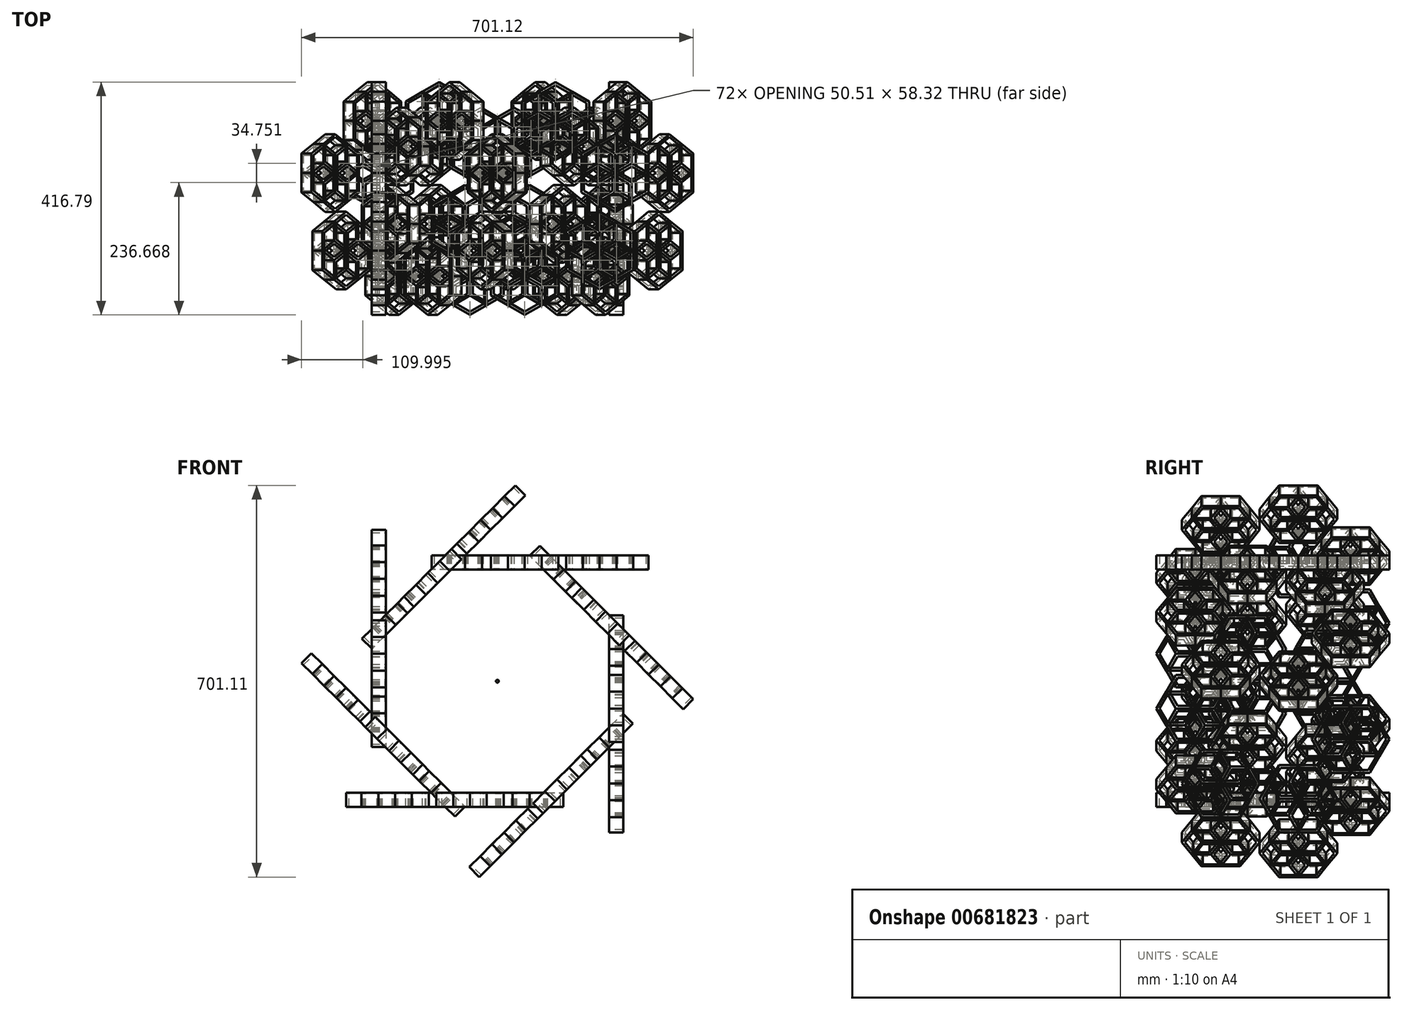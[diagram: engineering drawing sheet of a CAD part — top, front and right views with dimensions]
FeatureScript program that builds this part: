
annotation { "Feature Type Name" : "Feature", "Feature Type Description" : "" }
export const myFeature = defineFeature(function(context is Context, id is Id, definition is map)
    precondition{}
    {
        {
            var Q0;
            Q0=qCreatedBy(makeId("Top.planeOp"),FACE);
            var sketch = newSketch(context, id + "F0", { "sketchPlane" : qUnion([Q0])});
            skCircle(sketch, "E0.cCircle", {"center": v(0, 0) * mm, "radius": 34.75 * mm, "construction": true});
            skLineSegment(sketch, "E0.0", {"start": v(30.1, 17.38) * mm, "end": v(30.1, -17.38) * mm});
            skLineSegment(sketch, "E0.1", {"start": v(30.1, -17.38) * mm, "end": v(0, -34.75) * mm});
            skLineSegment(sketch, "E0.2", {"start": v(0, -34.75) * mm, "end": v(-30.1, -17.38) * mm});
            skLineSegment(sketch, "E0.3", {"start": v(-30.1, -17.38) * mm, "end": v(-30.1, 17.38) * mm});
            skLineSegment(sketch, "E0.4", {"start": v(-30.1, 17.38) * mm, "end": v(0, 34.75) * mm});
            skLineSegment(sketch, "E0.5", {"start": v(0, 34.75) * mm, "end": v(30.1, 17.38) * mm});
            skCircle(sketch, "E1.cCircle", {"center": v(0, 0) * mm, "radius": 29.16 * mm, "construction": true});
            skLineSegment(sketch, "E1.0", {"start": v(0, 29.16) * mm, "end": v(25.25, 14.58) * mm});
            skLineSegment(sketch, "E1.1", {"start": v(25.25, 14.58) * mm, "end": v(25.25, -14.58) * mm});
            skLineSegment(sketch, "E1.2", {"start": v(25.25, -14.58) * mm, "end": v(0, -29.16) * mm});
            skLineSegment(sketch, "E1.3", {"start": v(0, -29.16) * mm, "end": v(-25.25, -14.58) * mm});
            skLineSegment(sketch, "E1.4", {"start": v(-25.25, -14.58) * mm, "end": v(-25.25, 14.58) * mm});
            skLineSegment(sketch, "E1.5", {"start": v(-25.25, 14.58) * mm, "end": v(0, 29.16) * mm});
            skPoint(sketch, "E2", {"position": v(76.12, -75.54) * mm});
            skCircle(sketch, "E3", {"center": v(76.12, -75.54) * mm, "radius": 2.1 * mm});
            skSolve(sketch);
        }
        {
            var Q0;
            Q0=makeQuery(id+"F0.imprint","IMPRINT",FACE,{"disambiguationData":[TD([[makeQuery(id+"F0.imprint","IMPRINT",EDGE,{"derivedFrom":sQuery(id+"F0.wireOp",EDGE,"E0.0")}),-1.0]])]});
            extrude(context, id + "F1", {"entities" : qUnion([Q0]), "depth" : 25.4 * mm, "offsetDistance" : 25.4 * mm});
        }
        {
            var Q0;
            Q0=makeQuery(id+"F1.opExtrude","SWEPT_BODY",BODY,{"disambiguationData":[OSD([sQuery(id+"F0.wireOp",EDGE,"E0.0"),sQuery(id+"F0.wireOp",EDGE,"E0.1"),sQuery(id+"F0.wireOp",EDGE,"E0.2"),sQuery(id+"F0.wireOp",EDGE,"E0.3"),sQuery(id+"F0.wireOp",EDGE,"E0.4"),sQuery(id+"F0.wireOp",EDGE,"E0.5"),sQuery(id+"F0.wireOp",EDGE,"E1.0"),sQuery(id+"F0.wireOp",EDGE,"E1.1"),sQuery(id+"F0.wireOp",EDGE,"E1.2"),sQuery(id+"F0.wireOp",EDGE,"E1.3"),sQuery(id+"F0.wireOp",EDGE,"E1.4"),sQuery(id+"F0.wireOp",EDGE,"E1.5")])]});
            var Q1;
            Q1=makeQuery(id+"F1.opExtrude","SWEPT_EDGE",EDGE,{"disambiguationData":[OSD([sQuery(id+"F0.wireOp",EDGE,"E0.3"),sQuery(id+"F0.wireOp",EDGE,"E0.4")])]});
            circularPattern(context, id + "F2", {"entities" : qUnion([Q0]), "axis" : qUnion([Q1]), "angle" : 360 * degree, "instanceCount" : 6, "equalSpace" : true});
        }
        {
            var Q0;
            Q0=qCreatedBy(makeId("Top.planeOp"),FACE);
            var sketch = newSketch(context, id + "F3", { "sketchPlane" : qUnion([Q0])});
            skCircle(sketch, "E4", {"center": v(76.45, -75.87) * mm, "radius": 1.27 * mm});
            skSolve(sketch);
        }
        {
            var Q0;
            Q0=makeQuery(id+"F3.imprint","IMPRINT",FACE,{"disambiguationData":[TD([[makeQuery(id+"F3.imprint","IMPRINT",EDGE,{"derivedFrom":sQuery(id+"F3.wireOp",EDGE,"E4")}),1.0]])]});
            extrude(context, id + "F4", {"entities" : qUnion([Q0]), "depth" : 0.25 * mm, "offsetDistance" : 25.4 * mm});
        }
        {
            var Q0;
            Q0=makeQuery(id+"F1.opExtrude","SWEPT_BODY",BODY,{"disambiguationData":[OSD([sQuery(id+"F0.wireOp",EDGE,"E0.0"),sQuery(id+"F0.wireOp",EDGE,"E0.1"),sQuery(id+"F0.wireOp",EDGE,"E0.2"),sQuery(id+"F0.wireOp",EDGE,"E0.3"),sQuery(id+"F0.wireOp",EDGE,"E0.4"),sQuery(id+"F0.wireOp",EDGE,"E0.5"),sQuery(id+"F0.wireOp",EDGE,"E1.0"),sQuery(id+"F0.wireOp",EDGE,"E1.1"),sQuery(id+"F0.wireOp",EDGE,"E1.2"),sQuery(id+"F0.wireOp",EDGE,"E1.3"),sQuery(id+"F0.wireOp",EDGE,"E1.4"),sQuery(id+"F0.wireOp",EDGE,"E1.5")])]});
            var Q1;
            Q1=makeQuery(id+"F2.opPattern","COPY",BODY,{"derivedFrom":makeQuery(id+"F1.opExtrude","SWEPT_BODY",BODY,{"disambiguationData":[OSD([sQuery(id+"F0.wireOp",EDGE,"E0.0"),sQuery(id+"F0.wireOp",EDGE,"E0.1"),sQuery(id+"F0.wireOp",EDGE,"E0.2"),sQuery(id+"F0.wireOp",EDGE,"E0.3"),sQuery(id+"F0.wireOp",EDGE,"E0.4"),sQuery(id+"F0.wireOp",EDGE,"E0.5"),sQuery(id+"F0.wireOp",EDGE,"E1.0"),sQuery(id+"F0.wireOp",EDGE,"E1.1"),sQuery(id+"F0.wireOp",EDGE,"E1.2"),sQuery(id+"F0.wireOp",EDGE,"E1.3"),sQuery(id+"F0.wireOp",EDGE,"E1.4"),sQuery(id+"F0.wireOp",EDGE,"E1.5")])]}),"instanceName":"1"});
            var Q2;
            Q2=makeQuery(id+"F2.opPattern","COPY",BODY,{"derivedFrom":makeQuery(id+"F1.opExtrude","SWEPT_BODY",BODY,{"disambiguationData":[OSD([sQuery(id+"F0.wireOp",EDGE,"E0.0"),sQuery(id+"F0.wireOp",EDGE,"E0.1"),sQuery(id+"F0.wireOp",EDGE,"E0.2"),sQuery(id+"F0.wireOp",EDGE,"E0.3"),sQuery(id+"F0.wireOp",EDGE,"E0.4"),sQuery(id+"F0.wireOp",EDGE,"E0.5"),sQuery(id+"F0.wireOp",EDGE,"E1.0"),sQuery(id+"F0.wireOp",EDGE,"E1.1"),sQuery(id+"F0.wireOp",EDGE,"E1.2"),sQuery(id+"F0.wireOp",EDGE,"E1.3"),sQuery(id+"F0.wireOp",EDGE,"E1.4"),sQuery(id+"F0.wireOp",EDGE,"E1.5")])]}),"instanceName":"2"});
            var Q3;
            Q3=makeQuery(id+"F2.opPattern","COPY",BODY,{"derivedFrom":makeQuery(id+"F1.opExtrude","SWEPT_BODY",BODY,{"disambiguationData":[OSD([sQuery(id+"F0.wireOp",EDGE,"E0.0"),sQuery(id+"F0.wireOp",EDGE,"E0.1"),sQuery(id+"F0.wireOp",EDGE,"E0.2"),sQuery(id+"F0.wireOp",EDGE,"E0.3"),sQuery(id+"F0.wireOp",EDGE,"E0.4"),sQuery(id+"F0.wireOp",EDGE,"E0.5"),sQuery(id+"F0.wireOp",EDGE,"E1.0"),sQuery(id+"F0.wireOp",EDGE,"E1.1"),sQuery(id+"F0.wireOp",EDGE,"E1.2"),sQuery(id+"F0.wireOp",EDGE,"E1.3"),sQuery(id+"F0.wireOp",EDGE,"E1.4"),sQuery(id+"F0.wireOp",EDGE,"E1.5")])]}),"instanceName":"3"});
            var Q4;
            Q4=makeQuery(id+"F2.opPattern","COPY",BODY,{"derivedFrom":makeQuery(id+"F1.opExtrude","SWEPT_BODY",BODY,{"disambiguationData":[OSD([sQuery(id+"F0.wireOp",EDGE,"E0.0"),sQuery(id+"F0.wireOp",EDGE,"E0.1"),sQuery(id+"F0.wireOp",EDGE,"E0.2"),sQuery(id+"F0.wireOp",EDGE,"E0.3"),sQuery(id+"F0.wireOp",EDGE,"E0.4"),sQuery(id+"F0.wireOp",EDGE,"E0.5"),sQuery(id+"F0.wireOp",EDGE,"E1.0"),sQuery(id+"F0.wireOp",EDGE,"E1.1"),sQuery(id+"F0.wireOp",EDGE,"E1.2"),sQuery(id+"F0.wireOp",EDGE,"E1.3"),sQuery(id+"F0.wireOp",EDGE,"E1.4"),sQuery(id+"F0.wireOp",EDGE,"E1.5")])]}),"instanceName":"4"});
            var Q5;
            Q5=makeQuery(id+"F2.opPattern","COPY",BODY,{"derivedFrom":makeQuery(id+"F1.opExtrude","SWEPT_BODY",BODY,{"disambiguationData":[OSD([sQuery(id+"F0.wireOp",EDGE,"E0.0"),sQuery(id+"F0.wireOp",EDGE,"E0.1"),sQuery(id+"F0.wireOp",EDGE,"E0.2"),sQuery(id+"F0.wireOp",EDGE,"E0.3"),sQuery(id+"F0.wireOp",EDGE,"E0.4"),sQuery(id+"F0.wireOp",EDGE,"E0.5"),sQuery(id+"F0.wireOp",EDGE,"E1.0"),sQuery(id+"F0.wireOp",EDGE,"E1.1"),sQuery(id+"F0.wireOp",EDGE,"E1.2"),sQuery(id+"F0.wireOp",EDGE,"E1.3"),sQuery(id+"F0.wireOp",EDGE,"E1.4"),sQuery(id+"F0.wireOp",EDGE,"E1.5")])]}),"instanceName":"5"});
            var Q6;
            Q6=makeQuery(id+"F4.opExtrude","CAP_EDGE",EDGE,{"disambiguationData":[OSD([sQuery(id+"F3.wireOp",EDGE,"E4")])],"isStart":false});
            circularPattern(context, id + "F5", {"entities" : qUnion([Q0, Q1, Q2, Q3, Q4, Q5]), "axis" : qUnion([Q6]), "angle" : 360 * degree, "instanceCount" : 6, "oppositeDirection" : true, "equalSpace" : true});
        }
        {
            var Q0;
            Q0=qCreatedBy(makeId("Front.planeOp"),FACE);
            var sketch = newSketch(context, id + "F6", { "sketchPlane" : qUnion([Q0])});
            skCircle(sketch, "E5", {"center": v(0, -199.7) * mm, "radius": 2.54 * mm});
            skSolve(sketch);
        }
        {
            var Q0;
            Q0=makeQuery(id+"F6.imprint","IMPRINT",FACE,{"disambiguationData":[TD([[makeQuery(id+"F6.imprint","IMPRINT",EDGE,{"derivedFrom":sQuery(id+"F6.wireOp",EDGE,"E5")}),1.0]])]});
            extrude(context, id + "F7", {"entities" : qUnion([Q0]), "depth" : 0.25 * mm, "offsetDistance" : 25.4 * mm});
        }
        {
            var Q0;
            Q0=makeQuery(id+"F2.opPattern","COPY",BODY,{"derivedFrom":makeQuery(id+"F1.opExtrude","SWEPT_BODY",BODY,{"disambiguationData":[OSD([sQuery(id+"F0.wireOp",EDGE,"E0.0"),sQuery(id+"F0.wireOp",EDGE,"E0.1"),sQuery(id+"F0.wireOp",EDGE,"E0.2"),sQuery(id+"F0.wireOp",EDGE,"E0.3"),sQuery(id+"F0.wireOp",EDGE,"E0.4"),sQuery(id+"F0.wireOp",EDGE,"E0.5"),sQuery(id+"F0.wireOp",EDGE,"E1.0"),sQuery(id+"F0.wireOp",EDGE,"E1.1"),sQuery(id+"F0.wireOp",EDGE,"E1.2"),sQuery(id+"F0.wireOp",EDGE,"E1.3"),sQuery(id+"F0.wireOp",EDGE,"E1.4"),sQuery(id+"F0.wireOp",EDGE,"E1.5")])]}),"instanceName":"1"});
            var Q1;
            Q1=makeQuery(id+"F2.opPattern","COPY",BODY,{"derivedFrom":makeQuery(id+"F1.opExtrude","SWEPT_BODY",BODY,{"disambiguationData":[OSD([sQuery(id+"F0.wireOp",EDGE,"E0.0"),sQuery(id+"F0.wireOp",EDGE,"E0.1"),sQuery(id+"F0.wireOp",EDGE,"E0.2"),sQuery(id+"F0.wireOp",EDGE,"E0.3"),sQuery(id+"F0.wireOp",EDGE,"E0.4"),sQuery(id+"F0.wireOp",EDGE,"E0.5"),sQuery(id+"F0.wireOp",EDGE,"E1.0"),sQuery(id+"F0.wireOp",EDGE,"E1.1"),sQuery(id+"F0.wireOp",EDGE,"E1.2"),sQuery(id+"F0.wireOp",EDGE,"E1.3"),sQuery(id+"F0.wireOp",EDGE,"E1.4"),sQuery(id+"F0.wireOp",EDGE,"E1.5")])]}),"instanceName":"4"});
            var Q2;
            Q2=makeQuery(id+"F1.opExtrude","SWEPT_BODY",BODY,{"disambiguationData":[OSD([sQuery(id+"F0.wireOp",EDGE,"E0.0"),sQuery(id+"F0.wireOp",EDGE,"E0.1"),sQuery(id+"F0.wireOp",EDGE,"E0.2"),sQuery(id+"F0.wireOp",EDGE,"E0.3"),sQuery(id+"F0.wireOp",EDGE,"E0.4"),sQuery(id+"F0.wireOp",EDGE,"E0.5"),sQuery(id+"F0.wireOp",EDGE,"E1.0"),sQuery(id+"F0.wireOp",EDGE,"E1.1"),sQuery(id+"F0.wireOp",EDGE,"E1.2"),sQuery(id+"F0.wireOp",EDGE,"E1.3"),sQuery(id+"F0.wireOp",EDGE,"E1.4"),sQuery(id+"F0.wireOp",EDGE,"E1.5")])]});
            var Q3;
            Q3=makeQuery(id+"F2.opPattern","COPY",BODY,{"derivedFrom":makeQuery(id+"F1.opExtrude","SWEPT_BODY",BODY,{"disambiguationData":[OSD([sQuery(id+"F0.wireOp",EDGE,"E0.0"),sQuery(id+"F0.wireOp",EDGE,"E0.1"),sQuery(id+"F0.wireOp",EDGE,"E0.2"),sQuery(id+"F0.wireOp",EDGE,"E0.3"),sQuery(id+"F0.wireOp",EDGE,"E0.4"),sQuery(id+"F0.wireOp",EDGE,"E0.5"),sQuery(id+"F0.wireOp",EDGE,"E1.0"),sQuery(id+"F0.wireOp",EDGE,"E1.1"),sQuery(id+"F0.wireOp",EDGE,"E1.2"),sQuery(id+"F0.wireOp",EDGE,"E1.3"),sQuery(id+"F0.wireOp",EDGE,"E1.4"),sQuery(id+"F0.wireOp",EDGE,"E1.5")])]}),"instanceName":"2"});
            var Q4;
            Q4=makeQuery(id+"F2.opPattern","COPY",BODY,{"derivedFrom":makeQuery(id+"F1.opExtrude","SWEPT_BODY",BODY,{"disambiguationData":[OSD([sQuery(id+"F0.wireOp",EDGE,"E0.0"),sQuery(id+"F0.wireOp",EDGE,"E0.1"),sQuery(id+"F0.wireOp",EDGE,"E0.2"),sQuery(id+"F0.wireOp",EDGE,"E0.3"),sQuery(id+"F0.wireOp",EDGE,"E0.4"),sQuery(id+"F0.wireOp",EDGE,"E0.5"),sQuery(id+"F0.wireOp",EDGE,"E1.0"),sQuery(id+"F0.wireOp",EDGE,"E1.1"),sQuery(id+"F0.wireOp",EDGE,"E1.2"),sQuery(id+"F0.wireOp",EDGE,"E1.3"),sQuery(id+"F0.wireOp",EDGE,"E1.4"),sQuery(id+"F0.wireOp",EDGE,"E1.5")])]}),"instanceName":"3"});
            var Q5;
            Q5=makeQuery(id+"F2.opPattern","COPY",BODY,{"derivedFrom":makeQuery(id+"F1.opExtrude","SWEPT_BODY",BODY,{"disambiguationData":[OSD([sQuery(id+"F0.wireOp",EDGE,"E0.0"),sQuery(id+"F0.wireOp",EDGE,"E0.1"),sQuery(id+"F0.wireOp",EDGE,"E0.2"),sQuery(id+"F0.wireOp",EDGE,"E0.3"),sQuery(id+"F0.wireOp",EDGE,"E0.4"),sQuery(id+"F0.wireOp",EDGE,"E0.5"),sQuery(id+"F0.wireOp",EDGE,"E1.0"),sQuery(id+"F0.wireOp",EDGE,"E1.1"),sQuery(id+"F0.wireOp",EDGE,"E1.2"),sQuery(id+"F0.wireOp",EDGE,"E1.3"),sQuery(id+"F0.wireOp",EDGE,"E1.4"),sQuery(id+"F0.wireOp",EDGE,"E1.5")])]}),"instanceName":"5"});
            var Q6;
            Q6=makeQuery(id+"F5.opPattern","COPY",BODY,{"derivedFrom":makeQuery(id+"F1.opExtrude","SWEPT_BODY",BODY,{"disambiguationData":[OSD([sQuery(id+"F0.wireOp",EDGE,"E0.0"),sQuery(id+"F0.wireOp",EDGE,"E0.1"),sQuery(id+"F0.wireOp",EDGE,"E0.2"),sQuery(id+"F0.wireOp",EDGE,"E0.3"),sQuery(id+"F0.wireOp",EDGE,"E0.4"),sQuery(id+"F0.wireOp",EDGE,"E0.5"),sQuery(id+"F0.wireOp",EDGE,"E1.0"),sQuery(id+"F0.wireOp",EDGE,"E1.1"),sQuery(id+"F0.wireOp",EDGE,"E1.2"),sQuery(id+"F0.wireOp",EDGE,"E1.3"),sQuery(id+"F0.wireOp",EDGE,"E1.4"),sQuery(id+"F0.wireOp",EDGE,"E1.5")])]}),"instanceName":"1"});
            var Q7;
            Q7=makeQuery(id+"F4.opExtrude","SWEPT_BODY",BODY,{"disambiguationData":[OSD([sQuery(id+"F3.wireOp",EDGE,"E4")])]});
            var Q8;
            Q8=makeQuery(id+"F5.opPattern","COPY",BODY,{"derivedFrom":makeQuery(id+"F2.opPattern","COPY",BODY,{"derivedFrom":makeQuery(id+"F1.opExtrude","SWEPT_BODY",BODY,{"disambiguationData":[OSD([sQuery(id+"F0.wireOp",EDGE,"E0.0"),sQuery(id+"F0.wireOp",EDGE,"E0.1"),sQuery(id+"F0.wireOp",EDGE,"E0.2"),sQuery(id+"F0.wireOp",EDGE,"E0.3"),sQuery(id+"F0.wireOp",EDGE,"E0.4"),sQuery(id+"F0.wireOp",EDGE,"E0.5"),sQuery(id+"F0.wireOp",EDGE,"E1.0"),sQuery(id+"F0.wireOp",EDGE,"E1.1"),sQuery(id+"F0.wireOp",EDGE,"E1.2"),sQuery(id+"F0.wireOp",EDGE,"E1.3"),sQuery(id+"F0.wireOp",EDGE,"E1.4"),sQuery(id+"F0.wireOp",EDGE,"E1.5")])]}),"instanceName":"1"}),"instanceName":"1"});
            var Q9;
            Q9=makeQuery(id+"F5.opPattern","COPY",BODY,{"derivedFrom":makeQuery(id+"F2.opPattern","COPY",BODY,{"derivedFrom":makeQuery(id+"F1.opExtrude","SWEPT_BODY",BODY,{"disambiguationData":[OSD([sQuery(id+"F0.wireOp",EDGE,"E0.0"),sQuery(id+"F0.wireOp",EDGE,"E0.1"),sQuery(id+"F0.wireOp",EDGE,"E0.2"),sQuery(id+"F0.wireOp",EDGE,"E0.3"),sQuery(id+"F0.wireOp",EDGE,"E0.4"),sQuery(id+"F0.wireOp",EDGE,"E0.5"),sQuery(id+"F0.wireOp",EDGE,"E1.0"),sQuery(id+"F0.wireOp",EDGE,"E1.1"),sQuery(id+"F0.wireOp",EDGE,"E1.2"),sQuery(id+"F0.wireOp",EDGE,"E1.3"),sQuery(id+"F0.wireOp",EDGE,"E1.4"),sQuery(id+"F0.wireOp",EDGE,"E1.5")])]}),"instanceName":"2"}),"instanceName":"1"});
            var Q10;
            Q10=makeQuery(id+"F5.opPattern","COPY",BODY,{"derivedFrom":makeQuery(id+"F2.opPattern","COPY",BODY,{"derivedFrom":makeQuery(id+"F1.opExtrude","SWEPT_BODY",BODY,{"disambiguationData":[OSD([sQuery(id+"F0.wireOp",EDGE,"E0.0"),sQuery(id+"F0.wireOp",EDGE,"E0.1"),sQuery(id+"F0.wireOp",EDGE,"E0.2"),sQuery(id+"F0.wireOp",EDGE,"E0.3"),sQuery(id+"F0.wireOp",EDGE,"E0.4"),sQuery(id+"F0.wireOp",EDGE,"E0.5"),sQuery(id+"F0.wireOp",EDGE,"E1.0"),sQuery(id+"F0.wireOp",EDGE,"E1.1"),sQuery(id+"F0.wireOp",EDGE,"E1.2"),sQuery(id+"F0.wireOp",EDGE,"E1.3"),sQuery(id+"F0.wireOp",EDGE,"E1.4"),sQuery(id+"F0.wireOp",EDGE,"E1.5")])]}),"instanceName":"3"}),"instanceName":"1"});
            var Q11;
            Q11=makeQuery(id+"F5.opPattern","COPY",BODY,{"derivedFrom":makeQuery(id+"F2.opPattern","COPY",BODY,{"derivedFrom":makeQuery(id+"F1.opExtrude","SWEPT_BODY",BODY,{"disambiguationData":[OSD([sQuery(id+"F0.wireOp",EDGE,"E0.0"),sQuery(id+"F0.wireOp",EDGE,"E0.1"),sQuery(id+"F0.wireOp",EDGE,"E0.2"),sQuery(id+"F0.wireOp",EDGE,"E0.3"),sQuery(id+"F0.wireOp",EDGE,"E0.4"),sQuery(id+"F0.wireOp",EDGE,"E0.5"),sQuery(id+"F0.wireOp",EDGE,"E1.0"),sQuery(id+"F0.wireOp",EDGE,"E1.1"),sQuery(id+"F0.wireOp",EDGE,"E1.2"),sQuery(id+"F0.wireOp",EDGE,"E1.3"),sQuery(id+"F0.wireOp",EDGE,"E1.4"),sQuery(id+"F0.wireOp",EDGE,"E1.5")])]}),"instanceName":"4"}),"instanceName":"1"});
            var Q12;
            Q12=makeQuery(id+"F5.opPattern","COPY",BODY,{"derivedFrom":makeQuery(id+"F2.opPattern","COPY",BODY,{"derivedFrom":makeQuery(id+"F1.opExtrude","SWEPT_BODY",BODY,{"disambiguationData":[OSD([sQuery(id+"F0.wireOp",EDGE,"E0.0"),sQuery(id+"F0.wireOp",EDGE,"E0.1"),sQuery(id+"F0.wireOp",EDGE,"E0.2"),sQuery(id+"F0.wireOp",EDGE,"E0.3"),sQuery(id+"F0.wireOp",EDGE,"E0.4"),sQuery(id+"F0.wireOp",EDGE,"E0.5"),sQuery(id+"F0.wireOp",EDGE,"E1.0"),sQuery(id+"F0.wireOp",EDGE,"E1.1"),sQuery(id+"F0.wireOp",EDGE,"E1.2"),sQuery(id+"F0.wireOp",EDGE,"E1.3"),sQuery(id+"F0.wireOp",EDGE,"E1.4"),sQuery(id+"F0.wireOp",EDGE,"E1.5")])]}),"instanceName":"5"}),"instanceName":"1"});
            var Q13;
            Q13=makeQuery(id+"F5.opPattern","COPY",BODY,{"derivedFrom":makeQuery(id+"F1.opExtrude","SWEPT_BODY",BODY,{"disambiguationData":[OSD([sQuery(id+"F0.wireOp",EDGE,"E0.0"),sQuery(id+"F0.wireOp",EDGE,"E0.1"),sQuery(id+"F0.wireOp",EDGE,"E0.2"),sQuery(id+"F0.wireOp",EDGE,"E0.3"),sQuery(id+"F0.wireOp",EDGE,"E0.4"),sQuery(id+"F0.wireOp",EDGE,"E0.5"),sQuery(id+"F0.wireOp",EDGE,"E1.0"),sQuery(id+"F0.wireOp",EDGE,"E1.1"),sQuery(id+"F0.wireOp",EDGE,"E1.2"),sQuery(id+"F0.wireOp",EDGE,"E1.3"),sQuery(id+"F0.wireOp",EDGE,"E1.4"),sQuery(id+"F0.wireOp",EDGE,"E1.5")])]}),"instanceName":"2"});
            var Q14;
            Q14=makeQuery(id+"F5.opPattern","COPY",BODY,{"derivedFrom":makeQuery(id+"F2.opPattern","COPY",BODY,{"derivedFrom":makeQuery(id+"F1.opExtrude","SWEPT_BODY",BODY,{"disambiguationData":[OSD([sQuery(id+"F0.wireOp",EDGE,"E0.0"),sQuery(id+"F0.wireOp",EDGE,"E0.1"),sQuery(id+"F0.wireOp",EDGE,"E0.2"),sQuery(id+"F0.wireOp",EDGE,"E0.3"),sQuery(id+"F0.wireOp",EDGE,"E0.4"),sQuery(id+"F0.wireOp",EDGE,"E0.5"),sQuery(id+"F0.wireOp",EDGE,"E1.0"),sQuery(id+"F0.wireOp",EDGE,"E1.1"),sQuery(id+"F0.wireOp",EDGE,"E1.2"),sQuery(id+"F0.wireOp",EDGE,"E1.3"),sQuery(id+"F0.wireOp",EDGE,"E1.4"),sQuery(id+"F0.wireOp",EDGE,"E1.5")])]}),"instanceName":"1"}),"instanceName":"2"});
            var Q15;
            Q15=makeQuery(id+"F5.opPattern","COPY",BODY,{"derivedFrom":makeQuery(id+"F2.opPattern","COPY",BODY,{"derivedFrom":makeQuery(id+"F1.opExtrude","SWEPT_BODY",BODY,{"disambiguationData":[OSD([sQuery(id+"F0.wireOp",EDGE,"E0.0"),sQuery(id+"F0.wireOp",EDGE,"E0.1"),sQuery(id+"F0.wireOp",EDGE,"E0.2"),sQuery(id+"F0.wireOp",EDGE,"E0.3"),sQuery(id+"F0.wireOp",EDGE,"E0.4"),sQuery(id+"F0.wireOp",EDGE,"E0.5"),sQuery(id+"F0.wireOp",EDGE,"E1.0"),sQuery(id+"F0.wireOp",EDGE,"E1.1"),sQuery(id+"F0.wireOp",EDGE,"E1.2"),sQuery(id+"F0.wireOp",EDGE,"E1.3"),sQuery(id+"F0.wireOp",EDGE,"E1.4"),sQuery(id+"F0.wireOp",EDGE,"E1.5")])]}),"instanceName":"2"}),"instanceName":"2"});
            var Q16;
            Q16=makeQuery(id+"F5.opPattern","COPY",BODY,{"derivedFrom":makeQuery(id+"F2.opPattern","COPY",BODY,{"derivedFrom":makeQuery(id+"F1.opExtrude","SWEPT_BODY",BODY,{"disambiguationData":[OSD([sQuery(id+"F0.wireOp",EDGE,"E0.0"),sQuery(id+"F0.wireOp",EDGE,"E0.1"),sQuery(id+"F0.wireOp",EDGE,"E0.2"),sQuery(id+"F0.wireOp",EDGE,"E0.3"),sQuery(id+"F0.wireOp",EDGE,"E0.4"),sQuery(id+"F0.wireOp",EDGE,"E0.5"),sQuery(id+"F0.wireOp",EDGE,"E1.0"),sQuery(id+"F0.wireOp",EDGE,"E1.1"),sQuery(id+"F0.wireOp",EDGE,"E1.2"),sQuery(id+"F0.wireOp",EDGE,"E1.3"),sQuery(id+"F0.wireOp",EDGE,"E1.4"),sQuery(id+"F0.wireOp",EDGE,"E1.5")])]}),"instanceName":"3"}),"instanceName":"2"});
            var Q17;
            Q17=makeQuery(id+"F5.opPattern","COPY",BODY,{"derivedFrom":makeQuery(id+"F2.opPattern","COPY",BODY,{"derivedFrom":makeQuery(id+"F1.opExtrude","SWEPT_BODY",BODY,{"disambiguationData":[OSD([sQuery(id+"F0.wireOp",EDGE,"E0.0"),sQuery(id+"F0.wireOp",EDGE,"E0.1"),sQuery(id+"F0.wireOp",EDGE,"E0.2"),sQuery(id+"F0.wireOp",EDGE,"E0.3"),sQuery(id+"F0.wireOp",EDGE,"E0.4"),sQuery(id+"F0.wireOp",EDGE,"E0.5"),sQuery(id+"F0.wireOp",EDGE,"E1.0"),sQuery(id+"F0.wireOp",EDGE,"E1.1"),sQuery(id+"F0.wireOp",EDGE,"E1.2"),sQuery(id+"F0.wireOp",EDGE,"E1.3"),sQuery(id+"F0.wireOp",EDGE,"E1.4"),sQuery(id+"F0.wireOp",EDGE,"E1.5")])]}),"instanceName":"4"}),"instanceName":"2"});
            var Q18;
            Q18=makeQuery(id+"F5.opPattern","COPY",BODY,{"derivedFrom":makeQuery(id+"F2.opPattern","COPY",BODY,{"derivedFrom":makeQuery(id+"F1.opExtrude","SWEPT_BODY",BODY,{"disambiguationData":[OSD([sQuery(id+"F0.wireOp",EDGE,"E0.0"),sQuery(id+"F0.wireOp",EDGE,"E0.1"),sQuery(id+"F0.wireOp",EDGE,"E0.2"),sQuery(id+"F0.wireOp",EDGE,"E0.3"),sQuery(id+"F0.wireOp",EDGE,"E0.4"),sQuery(id+"F0.wireOp",EDGE,"E0.5"),sQuery(id+"F0.wireOp",EDGE,"E1.0"),sQuery(id+"F0.wireOp",EDGE,"E1.1"),sQuery(id+"F0.wireOp",EDGE,"E1.2"),sQuery(id+"F0.wireOp",EDGE,"E1.3"),sQuery(id+"F0.wireOp",EDGE,"E1.4"),sQuery(id+"F0.wireOp",EDGE,"E1.5")])]}),"instanceName":"5"}),"instanceName":"2"});
            var Q19;
            Q19=makeQuery(id+"F5.opPattern","COPY",BODY,{"derivedFrom":makeQuery(id+"F1.opExtrude","SWEPT_BODY",BODY,{"disambiguationData":[OSD([sQuery(id+"F0.wireOp",EDGE,"E0.0"),sQuery(id+"F0.wireOp",EDGE,"E0.1"),sQuery(id+"F0.wireOp",EDGE,"E0.2"),sQuery(id+"F0.wireOp",EDGE,"E0.3"),sQuery(id+"F0.wireOp",EDGE,"E0.4"),sQuery(id+"F0.wireOp",EDGE,"E0.5"),sQuery(id+"F0.wireOp",EDGE,"E1.0"),sQuery(id+"F0.wireOp",EDGE,"E1.1"),sQuery(id+"F0.wireOp",EDGE,"E1.2"),sQuery(id+"F0.wireOp",EDGE,"E1.3"),sQuery(id+"F0.wireOp",EDGE,"E1.4"),sQuery(id+"F0.wireOp",EDGE,"E1.5")])]}),"instanceName":"3"});
            var Q20;
            Q20=makeQuery(id+"F5.opPattern","COPY",BODY,{"derivedFrom":makeQuery(id+"F2.opPattern","COPY",BODY,{"derivedFrom":makeQuery(id+"F1.opExtrude","SWEPT_BODY",BODY,{"disambiguationData":[OSD([sQuery(id+"F0.wireOp",EDGE,"E0.0"),sQuery(id+"F0.wireOp",EDGE,"E0.1"),sQuery(id+"F0.wireOp",EDGE,"E0.2"),sQuery(id+"F0.wireOp",EDGE,"E0.3"),sQuery(id+"F0.wireOp",EDGE,"E0.4"),sQuery(id+"F0.wireOp",EDGE,"E0.5"),sQuery(id+"F0.wireOp",EDGE,"E1.0"),sQuery(id+"F0.wireOp",EDGE,"E1.1"),sQuery(id+"F0.wireOp",EDGE,"E1.2"),sQuery(id+"F0.wireOp",EDGE,"E1.3"),sQuery(id+"F0.wireOp",EDGE,"E1.4"),sQuery(id+"F0.wireOp",EDGE,"E1.5")])]}),"instanceName":"1"}),"instanceName":"3"});
            var Q21;
            Q21=makeQuery(id+"F5.opPattern","COPY",BODY,{"derivedFrom":makeQuery(id+"F2.opPattern","COPY",BODY,{"derivedFrom":makeQuery(id+"F1.opExtrude","SWEPT_BODY",BODY,{"disambiguationData":[OSD([sQuery(id+"F0.wireOp",EDGE,"E0.0"),sQuery(id+"F0.wireOp",EDGE,"E0.1"),sQuery(id+"F0.wireOp",EDGE,"E0.2"),sQuery(id+"F0.wireOp",EDGE,"E0.3"),sQuery(id+"F0.wireOp",EDGE,"E0.4"),sQuery(id+"F0.wireOp",EDGE,"E0.5"),sQuery(id+"F0.wireOp",EDGE,"E1.0"),sQuery(id+"F0.wireOp",EDGE,"E1.1"),sQuery(id+"F0.wireOp",EDGE,"E1.2"),sQuery(id+"F0.wireOp",EDGE,"E1.3"),sQuery(id+"F0.wireOp",EDGE,"E1.4"),sQuery(id+"F0.wireOp",EDGE,"E1.5")])]}),"instanceName":"2"}),"instanceName":"3"});
            var Q22;
            Q22=makeQuery(id+"F5.opPattern","COPY",BODY,{"derivedFrom":makeQuery(id+"F2.opPattern","COPY",BODY,{"derivedFrom":makeQuery(id+"F1.opExtrude","SWEPT_BODY",BODY,{"disambiguationData":[OSD([sQuery(id+"F0.wireOp",EDGE,"E0.0"),sQuery(id+"F0.wireOp",EDGE,"E0.1"),sQuery(id+"F0.wireOp",EDGE,"E0.2"),sQuery(id+"F0.wireOp",EDGE,"E0.3"),sQuery(id+"F0.wireOp",EDGE,"E0.4"),sQuery(id+"F0.wireOp",EDGE,"E0.5"),sQuery(id+"F0.wireOp",EDGE,"E1.0"),sQuery(id+"F0.wireOp",EDGE,"E1.1"),sQuery(id+"F0.wireOp",EDGE,"E1.2"),sQuery(id+"F0.wireOp",EDGE,"E1.3"),sQuery(id+"F0.wireOp",EDGE,"E1.4"),sQuery(id+"F0.wireOp",EDGE,"E1.5")])]}),"instanceName":"3"}),"instanceName":"3"});
            var Q23;
            Q23=makeQuery(id+"F5.opPattern","COPY",BODY,{"derivedFrom":makeQuery(id+"F2.opPattern","COPY",BODY,{"derivedFrom":makeQuery(id+"F1.opExtrude","SWEPT_BODY",BODY,{"disambiguationData":[OSD([sQuery(id+"F0.wireOp",EDGE,"E0.0"),sQuery(id+"F0.wireOp",EDGE,"E0.1"),sQuery(id+"F0.wireOp",EDGE,"E0.2"),sQuery(id+"F0.wireOp",EDGE,"E0.3"),sQuery(id+"F0.wireOp",EDGE,"E0.4"),sQuery(id+"F0.wireOp",EDGE,"E0.5"),sQuery(id+"F0.wireOp",EDGE,"E1.0"),sQuery(id+"F0.wireOp",EDGE,"E1.1"),sQuery(id+"F0.wireOp",EDGE,"E1.2"),sQuery(id+"F0.wireOp",EDGE,"E1.3"),sQuery(id+"F0.wireOp",EDGE,"E1.4"),sQuery(id+"F0.wireOp",EDGE,"E1.5")])]}),"instanceName":"4"}),"instanceName":"3"});
            var Q24;
            Q24=makeQuery(id+"F5.opPattern","COPY",BODY,{"derivedFrom":makeQuery(id+"F2.opPattern","COPY",BODY,{"derivedFrom":makeQuery(id+"F1.opExtrude","SWEPT_BODY",BODY,{"disambiguationData":[OSD([sQuery(id+"F0.wireOp",EDGE,"E0.0"),sQuery(id+"F0.wireOp",EDGE,"E0.1"),sQuery(id+"F0.wireOp",EDGE,"E0.2"),sQuery(id+"F0.wireOp",EDGE,"E0.3"),sQuery(id+"F0.wireOp",EDGE,"E0.4"),sQuery(id+"F0.wireOp",EDGE,"E0.5"),sQuery(id+"F0.wireOp",EDGE,"E1.0"),sQuery(id+"F0.wireOp",EDGE,"E1.1"),sQuery(id+"F0.wireOp",EDGE,"E1.2"),sQuery(id+"F0.wireOp",EDGE,"E1.3"),sQuery(id+"F0.wireOp",EDGE,"E1.4"),sQuery(id+"F0.wireOp",EDGE,"E1.5")])]}),"instanceName":"5"}),"instanceName":"3"});
            var Q25;
            Q25=makeQuery(id+"F5.opPattern","COPY",BODY,{"derivedFrom":makeQuery(id+"F1.opExtrude","SWEPT_BODY",BODY,{"disambiguationData":[OSD([sQuery(id+"F0.wireOp",EDGE,"E0.0"),sQuery(id+"F0.wireOp",EDGE,"E0.1"),sQuery(id+"F0.wireOp",EDGE,"E0.2"),sQuery(id+"F0.wireOp",EDGE,"E0.3"),sQuery(id+"F0.wireOp",EDGE,"E0.4"),sQuery(id+"F0.wireOp",EDGE,"E0.5"),sQuery(id+"F0.wireOp",EDGE,"E1.0"),sQuery(id+"F0.wireOp",EDGE,"E1.1"),sQuery(id+"F0.wireOp",EDGE,"E1.2"),sQuery(id+"F0.wireOp",EDGE,"E1.3"),sQuery(id+"F0.wireOp",EDGE,"E1.4"),sQuery(id+"F0.wireOp",EDGE,"E1.5")])]}),"instanceName":"4"});
            var Q26;
            Q26=makeQuery(id+"F5.opPattern","COPY",BODY,{"derivedFrom":makeQuery(id+"F2.opPattern","COPY",BODY,{"derivedFrom":makeQuery(id+"F1.opExtrude","SWEPT_BODY",BODY,{"disambiguationData":[OSD([sQuery(id+"F0.wireOp",EDGE,"E0.0"),sQuery(id+"F0.wireOp",EDGE,"E0.1"),sQuery(id+"F0.wireOp",EDGE,"E0.2"),sQuery(id+"F0.wireOp",EDGE,"E0.3"),sQuery(id+"F0.wireOp",EDGE,"E0.4"),sQuery(id+"F0.wireOp",EDGE,"E0.5"),sQuery(id+"F0.wireOp",EDGE,"E1.0"),sQuery(id+"F0.wireOp",EDGE,"E1.1"),sQuery(id+"F0.wireOp",EDGE,"E1.2"),sQuery(id+"F0.wireOp",EDGE,"E1.3"),sQuery(id+"F0.wireOp",EDGE,"E1.4"),sQuery(id+"F0.wireOp",EDGE,"E1.5")])]}),"instanceName":"1"}),"instanceName":"4"});
            var Q27;
            Q27=makeQuery(id+"F5.opPattern","COPY",BODY,{"derivedFrom":makeQuery(id+"F2.opPattern","COPY",BODY,{"derivedFrom":makeQuery(id+"F1.opExtrude","SWEPT_BODY",BODY,{"disambiguationData":[OSD([sQuery(id+"F0.wireOp",EDGE,"E0.0"),sQuery(id+"F0.wireOp",EDGE,"E0.1"),sQuery(id+"F0.wireOp",EDGE,"E0.2"),sQuery(id+"F0.wireOp",EDGE,"E0.3"),sQuery(id+"F0.wireOp",EDGE,"E0.4"),sQuery(id+"F0.wireOp",EDGE,"E0.5"),sQuery(id+"F0.wireOp",EDGE,"E1.0"),sQuery(id+"F0.wireOp",EDGE,"E1.1"),sQuery(id+"F0.wireOp",EDGE,"E1.2"),sQuery(id+"F0.wireOp",EDGE,"E1.3"),sQuery(id+"F0.wireOp",EDGE,"E1.4"),sQuery(id+"F0.wireOp",EDGE,"E1.5")])]}),"instanceName":"2"}),"instanceName":"4"});
            var Q28;
            Q28=makeQuery(id+"F5.opPattern","COPY",BODY,{"derivedFrom":makeQuery(id+"F2.opPattern","COPY",BODY,{"derivedFrom":makeQuery(id+"F1.opExtrude","SWEPT_BODY",BODY,{"disambiguationData":[OSD([sQuery(id+"F0.wireOp",EDGE,"E0.0"),sQuery(id+"F0.wireOp",EDGE,"E0.1"),sQuery(id+"F0.wireOp",EDGE,"E0.2"),sQuery(id+"F0.wireOp",EDGE,"E0.3"),sQuery(id+"F0.wireOp",EDGE,"E0.4"),sQuery(id+"F0.wireOp",EDGE,"E0.5"),sQuery(id+"F0.wireOp",EDGE,"E1.0"),sQuery(id+"F0.wireOp",EDGE,"E1.1"),sQuery(id+"F0.wireOp",EDGE,"E1.2"),sQuery(id+"F0.wireOp",EDGE,"E1.3"),sQuery(id+"F0.wireOp",EDGE,"E1.4"),sQuery(id+"F0.wireOp",EDGE,"E1.5")])]}),"instanceName":"3"}),"instanceName":"4"});
            var Q29;
            Q29=makeQuery(id+"F5.opPattern","COPY",BODY,{"derivedFrom":makeQuery(id+"F2.opPattern","COPY",BODY,{"derivedFrom":makeQuery(id+"F1.opExtrude","SWEPT_BODY",BODY,{"disambiguationData":[OSD([sQuery(id+"F0.wireOp",EDGE,"E0.0"),sQuery(id+"F0.wireOp",EDGE,"E0.1"),sQuery(id+"F0.wireOp",EDGE,"E0.2"),sQuery(id+"F0.wireOp",EDGE,"E0.3"),sQuery(id+"F0.wireOp",EDGE,"E0.4"),sQuery(id+"F0.wireOp",EDGE,"E0.5"),sQuery(id+"F0.wireOp",EDGE,"E1.0"),sQuery(id+"F0.wireOp",EDGE,"E1.1"),sQuery(id+"F0.wireOp",EDGE,"E1.2"),sQuery(id+"F0.wireOp",EDGE,"E1.3"),sQuery(id+"F0.wireOp",EDGE,"E1.4"),sQuery(id+"F0.wireOp",EDGE,"E1.5")])]}),"instanceName":"4"}),"instanceName":"4"});
            var Q30;
            Q30=makeQuery(id+"F5.opPattern","COPY",BODY,{"derivedFrom":makeQuery(id+"F2.opPattern","COPY",BODY,{"derivedFrom":makeQuery(id+"F1.opExtrude","SWEPT_BODY",BODY,{"disambiguationData":[OSD([sQuery(id+"F0.wireOp",EDGE,"E0.0"),sQuery(id+"F0.wireOp",EDGE,"E0.1"),sQuery(id+"F0.wireOp",EDGE,"E0.2"),sQuery(id+"F0.wireOp",EDGE,"E0.3"),sQuery(id+"F0.wireOp",EDGE,"E0.4"),sQuery(id+"F0.wireOp",EDGE,"E0.5"),sQuery(id+"F0.wireOp",EDGE,"E1.0"),sQuery(id+"F0.wireOp",EDGE,"E1.1"),sQuery(id+"F0.wireOp",EDGE,"E1.2"),sQuery(id+"F0.wireOp",EDGE,"E1.3"),sQuery(id+"F0.wireOp",EDGE,"E1.4"),sQuery(id+"F0.wireOp",EDGE,"E1.5")])]}),"instanceName":"5"}),"instanceName":"4"});
            var Q31;
            Q31=makeQuery(id+"F5.opPattern","COPY",BODY,{"derivedFrom":makeQuery(id+"F1.opExtrude","SWEPT_BODY",BODY,{"disambiguationData":[OSD([sQuery(id+"F0.wireOp",EDGE,"E0.0"),sQuery(id+"F0.wireOp",EDGE,"E0.1"),sQuery(id+"F0.wireOp",EDGE,"E0.2"),sQuery(id+"F0.wireOp",EDGE,"E0.3"),sQuery(id+"F0.wireOp",EDGE,"E0.4"),sQuery(id+"F0.wireOp",EDGE,"E0.5"),sQuery(id+"F0.wireOp",EDGE,"E1.0"),sQuery(id+"F0.wireOp",EDGE,"E1.1"),sQuery(id+"F0.wireOp",EDGE,"E1.2"),sQuery(id+"F0.wireOp",EDGE,"E1.3"),sQuery(id+"F0.wireOp",EDGE,"E1.4"),sQuery(id+"F0.wireOp",EDGE,"E1.5")])]}),"instanceName":"5"});
            var Q32;
            Q32=makeQuery(id+"F5.opPattern","COPY",BODY,{"derivedFrom":makeQuery(id+"F2.opPattern","COPY",BODY,{"derivedFrom":makeQuery(id+"F1.opExtrude","SWEPT_BODY",BODY,{"disambiguationData":[OSD([sQuery(id+"F0.wireOp",EDGE,"E0.0"),sQuery(id+"F0.wireOp",EDGE,"E0.1"),sQuery(id+"F0.wireOp",EDGE,"E0.2"),sQuery(id+"F0.wireOp",EDGE,"E0.3"),sQuery(id+"F0.wireOp",EDGE,"E0.4"),sQuery(id+"F0.wireOp",EDGE,"E0.5"),sQuery(id+"F0.wireOp",EDGE,"E1.0"),sQuery(id+"F0.wireOp",EDGE,"E1.1"),sQuery(id+"F0.wireOp",EDGE,"E1.2"),sQuery(id+"F0.wireOp",EDGE,"E1.3"),sQuery(id+"F0.wireOp",EDGE,"E1.4"),sQuery(id+"F0.wireOp",EDGE,"E1.5")])]}),"instanceName":"1"}),"instanceName":"5"});
            var Q33;
            Q33=makeQuery(id+"F5.opPattern","COPY",BODY,{"derivedFrom":makeQuery(id+"F2.opPattern","COPY",BODY,{"derivedFrom":makeQuery(id+"F1.opExtrude","SWEPT_BODY",BODY,{"disambiguationData":[OSD([sQuery(id+"F0.wireOp",EDGE,"E0.0"),sQuery(id+"F0.wireOp",EDGE,"E0.1"),sQuery(id+"F0.wireOp",EDGE,"E0.2"),sQuery(id+"F0.wireOp",EDGE,"E0.3"),sQuery(id+"F0.wireOp",EDGE,"E0.4"),sQuery(id+"F0.wireOp",EDGE,"E0.5"),sQuery(id+"F0.wireOp",EDGE,"E1.0"),sQuery(id+"F0.wireOp",EDGE,"E1.1"),sQuery(id+"F0.wireOp",EDGE,"E1.2"),sQuery(id+"F0.wireOp",EDGE,"E1.3"),sQuery(id+"F0.wireOp",EDGE,"E1.4"),sQuery(id+"F0.wireOp",EDGE,"E1.5")])]}),"instanceName":"5"}),"instanceName":"5"});
            var Q34;
            Q34=makeQuery(id+"F5.opPattern","COPY",BODY,{"derivedFrom":makeQuery(id+"F1.opExtrude","SWEPT_BODY",BODY,{"disambiguationData":[OSD([sQuery(id+"F0.wireOp",EDGE,"E0.0"),sQuery(id+"F0.wireOp",EDGE,"E0.1"),sQuery(id+"F0.wireOp",EDGE,"E0.2"),sQuery(id+"F0.wireOp",EDGE,"E0.3"),sQuery(id+"F0.wireOp",EDGE,"E0.4"),sQuery(id+"F0.wireOp",EDGE,"E0.5"),sQuery(id+"F0.wireOp",EDGE,"E1.0"),sQuery(id+"F0.wireOp",EDGE,"E1.1"),sQuery(id+"F0.wireOp",EDGE,"E1.2"),sQuery(id+"F0.wireOp",EDGE,"E1.3"),sQuery(id+"F0.wireOp",EDGE,"E1.4"),sQuery(id+"F0.wireOp",EDGE,"E1.5")])]}),"instanceName":"6"});
            var Q35;
            Q35=makeQuery(id+"F5.opPattern","COPY",BODY,{"derivedFrom":makeQuery(id+"F2.opPattern","COPY",BODY,{"derivedFrom":makeQuery(id+"F1.opExtrude","SWEPT_BODY",BODY,{"disambiguationData":[OSD([sQuery(id+"F0.wireOp",EDGE,"E0.0"),sQuery(id+"F0.wireOp",EDGE,"E0.1"),sQuery(id+"F0.wireOp",EDGE,"E0.2"),sQuery(id+"F0.wireOp",EDGE,"E0.3"),sQuery(id+"F0.wireOp",EDGE,"E0.4"),sQuery(id+"F0.wireOp",EDGE,"E0.5"),sQuery(id+"F0.wireOp",EDGE,"E1.0"),sQuery(id+"F0.wireOp",EDGE,"E1.1"),sQuery(id+"F0.wireOp",EDGE,"E1.2"),sQuery(id+"F0.wireOp",EDGE,"E1.3"),sQuery(id+"F0.wireOp",EDGE,"E1.4"),sQuery(id+"F0.wireOp",EDGE,"E1.5")])]}),"instanceName":"1"}),"instanceName":"6"});
            var Q36;
            Q36=makeQuery(id+"F5.opPattern","COPY",BODY,{"derivedFrom":makeQuery(id+"F2.opPattern","COPY",BODY,{"derivedFrom":makeQuery(id+"F1.opExtrude","SWEPT_BODY",BODY,{"disambiguationData":[OSD([sQuery(id+"F0.wireOp",EDGE,"E0.0"),sQuery(id+"F0.wireOp",EDGE,"E0.1"),sQuery(id+"F0.wireOp",EDGE,"E0.2"),sQuery(id+"F0.wireOp",EDGE,"E0.3"),sQuery(id+"F0.wireOp",EDGE,"E0.4"),sQuery(id+"F0.wireOp",EDGE,"E0.5"),sQuery(id+"F0.wireOp",EDGE,"E1.0"),sQuery(id+"F0.wireOp",EDGE,"E1.1"),sQuery(id+"F0.wireOp",EDGE,"E1.2"),sQuery(id+"F0.wireOp",EDGE,"E1.3"),sQuery(id+"F0.wireOp",EDGE,"E1.4"),sQuery(id+"F0.wireOp",EDGE,"E1.5")])]}),"instanceName":"2"}),"instanceName":"6"});
            var Q37;
            Q37=makeQuery(id+"F5.opPattern","COPY",BODY,{"derivedFrom":makeQuery(id+"F2.opPattern","COPY",BODY,{"derivedFrom":makeQuery(id+"F1.opExtrude","SWEPT_BODY",BODY,{"disambiguationData":[OSD([sQuery(id+"F0.wireOp",EDGE,"E0.0"),sQuery(id+"F0.wireOp",EDGE,"E0.1"),sQuery(id+"F0.wireOp",EDGE,"E0.2"),sQuery(id+"F0.wireOp",EDGE,"E0.3"),sQuery(id+"F0.wireOp",EDGE,"E0.4"),sQuery(id+"F0.wireOp",EDGE,"E0.5"),sQuery(id+"F0.wireOp",EDGE,"E1.0"),sQuery(id+"F0.wireOp",EDGE,"E1.1"),sQuery(id+"F0.wireOp",EDGE,"E1.2"),sQuery(id+"F0.wireOp",EDGE,"E1.3"),sQuery(id+"F0.wireOp",EDGE,"E1.4"),sQuery(id+"F0.wireOp",EDGE,"E1.5")])]}),"instanceName":"3"}),"instanceName":"6"});
            var Q38;
            Q38=makeQuery(id+"F5.opPattern","COPY",BODY,{"derivedFrom":makeQuery(id+"F2.opPattern","COPY",BODY,{"derivedFrom":makeQuery(id+"F1.opExtrude","SWEPT_BODY",BODY,{"disambiguationData":[OSD([sQuery(id+"F0.wireOp",EDGE,"E0.0"),sQuery(id+"F0.wireOp",EDGE,"E0.1"),sQuery(id+"F0.wireOp",EDGE,"E0.2"),sQuery(id+"F0.wireOp",EDGE,"E0.3"),sQuery(id+"F0.wireOp",EDGE,"E0.4"),sQuery(id+"F0.wireOp",EDGE,"E0.5"),sQuery(id+"F0.wireOp",EDGE,"E1.0"),sQuery(id+"F0.wireOp",EDGE,"E1.1"),sQuery(id+"F0.wireOp",EDGE,"E1.2"),sQuery(id+"F0.wireOp",EDGE,"E1.3"),sQuery(id+"F0.wireOp",EDGE,"E1.4"),sQuery(id+"F0.wireOp",EDGE,"E1.5")])]}),"instanceName":"4"}),"instanceName":"6"});
            var Q39;
            Q39=makeQuery(id+"F5.opPattern","COPY",BODY,{"derivedFrom":makeQuery(id+"F2.opPattern","COPY",BODY,{"derivedFrom":makeQuery(id+"F1.opExtrude","SWEPT_BODY",BODY,{"disambiguationData":[OSD([sQuery(id+"F0.wireOp",EDGE,"E0.0"),sQuery(id+"F0.wireOp",EDGE,"E0.1"),sQuery(id+"F0.wireOp",EDGE,"E0.2"),sQuery(id+"F0.wireOp",EDGE,"E0.3"),sQuery(id+"F0.wireOp",EDGE,"E0.4"),sQuery(id+"F0.wireOp",EDGE,"E0.5"),sQuery(id+"F0.wireOp",EDGE,"E1.0"),sQuery(id+"F0.wireOp",EDGE,"E1.1"),sQuery(id+"F0.wireOp",EDGE,"E1.2"),sQuery(id+"F0.wireOp",EDGE,"E1.3"),sQuery(id+"F0.wireOp",EDGE,"E1.4"),sQuery(id+"F0.wireOp",EDGE,"E1.5")])]}),"instanceName":"5"}),"instanceName":"6"});
            var Q40;
            Q40=makeQuery(id+"F5.opPattern","COPY",BODY,{"derivedFrom":makeQuery(id+"F1.opExtrude","SWEPT_BODY",BODY,{"disambiguationData":[OSD([sQuery(id+"F0.wireOp",EDGE,"E0.0"),sQuery(id+"F0.wireOp",EDGE,"E0.1"),sQuery(id+"F0.wireOp",EDGE,"E0.2"),sQuery(id+"F0.wireOp",EDGE,"E0.3"),sQuery(id+"F0.wireOp",EDGE,"E0.4"),sQuery(id+"F0.wireOp",EDGE,"E0.5"),sQuery(id+"F0.wireOp",EDGE,"E1.0"),sQuery(id+"F0.wireOp",EDGE,"E1.1"),sQuery(id+"F0.wireOp",EDGE,"E1.2"),sQuery(id+"F0.wireOp",EDGE,"E1.3"),sQuery(id+"F0.wireOp",EDGE,"E1.4"),sQuery(id+"F0.wireOp",EDGE,"E1.5")])]}),"instanceName":"7"});
            var Q41;
            Q41=makeQuery(id+"F5.opPattern","COPY",BODY,{"derivedFrom":makeQuery(id+"F2.opPattern","COPY",BODY,{"derivedFrom":makeQuery(id+"F1.opExtrude","SWEPT_BODY",BODY,{"disambiguationData":[OSD([sQuery(id+"F0.wireOp",EDGE,"E0.0"),sQuery(id+"F0.wireOp",EDGE,"E0.1"),sQuery(id+"F0.wireOp",EDGE,"E0.2"),sQuery(id+"F0.wireOp",EDGE,"E0.3"),sQuery(id+"F0.wireOp",EDGE,"E0.4"),sQuery(id+"F0.wireOp",EDGE,"E0.5"),sQuery(id+"F0.wireOp",EDGE,"E1.0"),sQuery(id+"F0.wireOp",EDGE,"E1.1"),sQuery(id+"F0.wireOp",EDGE,"E1.2"),sQuery(id+"F0.wireOp",EDGE,"E1.3"),sQuery(id+"F0.wireOp",EDGE,"E1.4"),sQuery(id+"F0.wireOp",EDGE,"E1.5")])]}),"instanceName":"1"}),"instanceName":"7"});
            var Q42;
            Q42=makeQuery(id+"F5.opPattern","COPY",BODY,{"derivedFrom":makeQuery(id+"F2.opPattern","COPY",BODY,{"derivedFrom":makeQuery(id+"F1.opExtrude","SWEPT_BODY",BODY,{"disambiguationData":[OSD([sQuery(id+"F0.wireOp",EDGE,"E0.0"),sQuery(id+"F0.wireOp",EDGE,"E0.1"),sQuery(id+"F0.wireOp",EDGE,"E0.2"),sQuery(id+"F0.wireOp",EDGE,"E0.3"),sQuery(id+"F0.wireOp",EDGE,"E0.4"),sQuery(id+"F0.wireOp",EDGE,"E0.5"),sQuery(id+"F0.wireOp",EDGE,"E1.0"),sQuery(id+"F0.wireOp",EDGE,"E1.1"),sQuery(id+"F0.wireOp",EDGE,"E1.2"),sQuery(id+"F0.wireOp",EDGE,"E1.3"),sQuery(id+"F0.wireOp",EDGE,"E1.4"),sQuery(id+"F0.wireOp",EDGE,"E1.5")])]}),"instanceName":"2"}),"instanceName":"7"});
            var Q43;
            Q43=makeQuery(id+"F5.opPattern","COPY",BODY,{"derivedFrom":makeQuery(id+"F2.opPattern","COPY",BODY,{"derivedFrom":makeQuery(id+"F1.opExtrude","SWEPT_BODY",BODY,{"disambiguationData":[OSD([sQuery(id+"F0.wireOp",EDGE,"E0.0"),sQuery(id+"F0.wireOp",EDGE,"E0.1"),sQuery(id+"F0.wireOp",EDGE,"E0.2"),sQuery(id+"F0.wireOp",EDGE,"E0.3"),sQuery(id+"F0.wireOp",EDGE,"E0.4"),sQuery(id+"F0.wireOp",EDGE,"E0.5"),sQuery(id+"F0.wireOp",EDGE,"E1.0"),sQuery(id+"F0.wireOp",EDGE,"E1.1"),sQuery(id+"F0.wireOp",EDGE,"E1.2"),sQuery(id+"F0.wireOp",EDGE,"E1.3"),sQuery(id+"F0.wireOp",EDGE,"E1.4"),sQuery(id+"F0.wireOp",EDGE,"E1.5")])]}),"instanceName":"3"}),"instanceName":"7"});
            var Q44;
            Q44=makeQuery(id+"F5.opPattern","COPY",BODY,{"derivedFrom":makeQuery(id+"F2.opPattern","COPY",BODY,{"derivedFrom":makeQuery(id+"F1.opExtrude","SWEPT_BODY",BODY,{"disambiguationData":[OSD([sQuery(id+"F0.wireOp",EDGE,"E0.0"),sQuery(id+"F0.wireOp",EDGE,"E0.1"),sQuery(id+"F0.wireOp",EDGE,"E0.2"),sQuery(id+"F0.wireOp",EDGE,"E0.3"),sQuery(id+"F0.wireOp",EDGE,"E0.4"),sQuery(id+"F0.wireOp",EDGE,"E0.5"),sQuery(id+"F0.wireOp",EDGE,"E1.0"),sQuery(id+"F0.wireOp",EDGE,"E1.1"),sQuery(id+"F0.wireOp",EDGE,"E1.2"),sQuery(id+"F0.wireOp",EDGE,"E1.3"),sQuery(id+"F0.wireOp",EDGE,"E1.4"),sQuery(id+"F0.wireOp",EDGE,"E1.5")])]}),"instanceName":"4"}),"instanceName":"7"});
            var Q45;
            Q45=makeQuery(id+"F5.opPattern","COPY",BODY,{"derivedFrom":makeQuery(id+"F2.opPattern","COPY",BODY,{"derivedFrom":makeQuery(id+"F1.opExtrude","SWEPT_BODY",BODY,{"disambiguationData":[OSD([sQuery(id+"F0.wireOp",EDGE,"E0.0"),sQuery(id+"F0.wireOp",EDGE,"E0.1"),sQuery(id+"F0.wireOp",EDGE,"E0.2"),sQuery(id+"F0.wireOp",EDGE,"E0.3"),sQuery(id+"F0.wireOp",EDGE,"E0.4"),sQuery(id+"F0.wireOp",EDGE,"E0.5"),sQuery(id+"F0.wireOp",EDGE,"E1.0"),sQuery(id+"F0.wireOp",EDGE,"E1.1"),sQuery(id+"F0.wireOp",EDGE,"E1.2"),sQuery(id+"F0.wireOp",EDGE,"E1.3"),sQuery(id+"F0.wireOp",EDGE,"E1.4"),sQuery(id+"F0.wireOp",EDGE,"E1.5")])]}),"instanceName":"5"}),"instanceName":"7"});
            var Q46;
            Q46=makeQuery(id+"F7.opExtrude","SWEPT_BODY",BODY,{"disambiguationData":[OSD([sQuery(id+"F6.wireOp",EDGE,"E5")])]});
            var Q47;
            Q47=makeQuery(id+"F5.opPattern","COPY",BODY,{"derivedFrom":makeQuery(id+"F2.opPattern","COPY",BODY,{"derivedFrom":makeQuery(id+"F1.opExtrude","SWEPT_BODY",BODY,{"disambiguationData":[OSD([sQuery(id+"F0.wireOp",EDGE,"E0.0"),sQuery(id+"F0.wireOp",EDGE,"E0.1"),sQuery(id+"F0.wireOp",EDGE,"E0.2"),sQuery(id+"F0.wireOp",EDGE,"E0.3"),sQuery(id+"F0.wireOp",EDGE,"E0.4"),sQuery(id+"F0.wireOp",EDGE,"E0.5"),sQuery(id+"F0.wireOp",EDGE,"E1.0"),sQuery(id+"F0.wireOp",EDGE,"E1.1"),sQuery(id+"F0.wireOp",EDGE,"E1.2"),sQuery(id+"F0.wireOp",EDGE,"E1.3"),sQuery(id+"F0.wireOp",EDGE,"E1.4"),sQuery(id+"F0.wireOp",EDGE,"E1.5")])]}),"instanceName":"2"}),"instanceName":"5"});
            var Q48;
            Q48=makeQuery(id+"F5.opPattern","COPY",BODY,{"derivedFrom":makeQuery(id+"F2.opPattern","COPY",BODY,{"derivedFrom":makeQuery(id+"F1.opExtrude","SWEPT_BODY",BODY,{"disambiguationData":[OSD([sQuery(id+"F0.wireOp",EDGE,"E0.0"),sQuery(id+"F0.wireOp",EDGE,"E0.1"),sQuery(id+"F0.wireOp",EDGE,"E0.2"),sQuery(id+"F0.wireOp",EDGE,"E0.3"),sQuery(id+"F0.wireOp",EDGE,"E0.4"),sQuery(id+"F0.wireOp",EDGE,"E0.5"),sQuery(id+"F0.wireOp",EDGE,"E1.0"),sQuery(id+"F0.wireOp",EDGE,"E1.1"),sQuery(id+"F0.wireOp",EDGE,"E1.2"),sQuery(id+"F0.wireOp",EDGE,"E1.3"),sQuery(id+"F0.wireOp",EDGE,"E1.4"),sQuery(id+"F0.wireOp",EDGE,"E1.5")])]}),"instanceName":"3"}),"instanceName":"5"});
            var Q49;
            Q49=makeQuery(id+"F5.opPattern","COPY",BODY,{"derivedFrom":makeQuery(id+"F2.opPattern","COPY",BODY,{"derivedFrom":makeQuery(id+"F1.opExtrude","SWEPT_BODY",BODY,{"disambiguationData":[OSD([sQuery(id+"F0.wireOp",EDGE,"E0.0"),sQuery(id+"F0.wireOp",EDGE,"E0.1"),sQuery(id+"F0.wireOp",EDGE,"E0.2"),sQuery(id+"F0.wireOp",EDGE,"E0.3"),sQuery(id+"F0.wireOp",EDGE,"E0.4"),sQuery(id+"F0.wireOp",EDGE,"E0.5"),sQuery(id+"F0.wireOp",EDGE,"E1.0"),sQuery(id+"F0.wireOp",EDGE,"E1.1"),sQuery(id+"F0.wireOp",EDGE,"E1.2"),sQuery(id+"F0.wireOp",EDGE,"E1.3"),sQuery(id+"F0.wireOp",EDGE,"E1.4"),sQuery(id+"F0.wireOp",EDGE,"E1.5")])]}),"instanceName":"4"}),"instanceName":"5"});
            var Q50;
            Q50=makeQuery(id+"F7.opExtrude","CAP_EDGE",EDGE,{"disambiguationData":[OSD([sQuery(id+"F6.wireOp",EDGE,"E5")])],"isStart":false});
            circularPattern(context, id + "F8", {"entities" : qUnion([Q0, Q1, Q2, Q3, Q4, Q5, Q6, Q7, Q8, Q9, Q10, Q11, Q12, Q13, Q14, Q15, Q16, Q17, Q18, Q19, Q20, Q21, Q22, Q23, Q24, Q25, Q26, Q27, Q28, Q29, Q30, Q31, Q32, Q33, Q34, Q35, Q36, Q37, Q38, Q39, Q40, Q41, Q42, Q43, Q44, Q45, Q46, Q47, Q48, Q49]), "axis" : qUnion([Q50]), "angle" : 360 * degree, "instanceCount" : 8, "equalSpace" : true});
        }
    });
